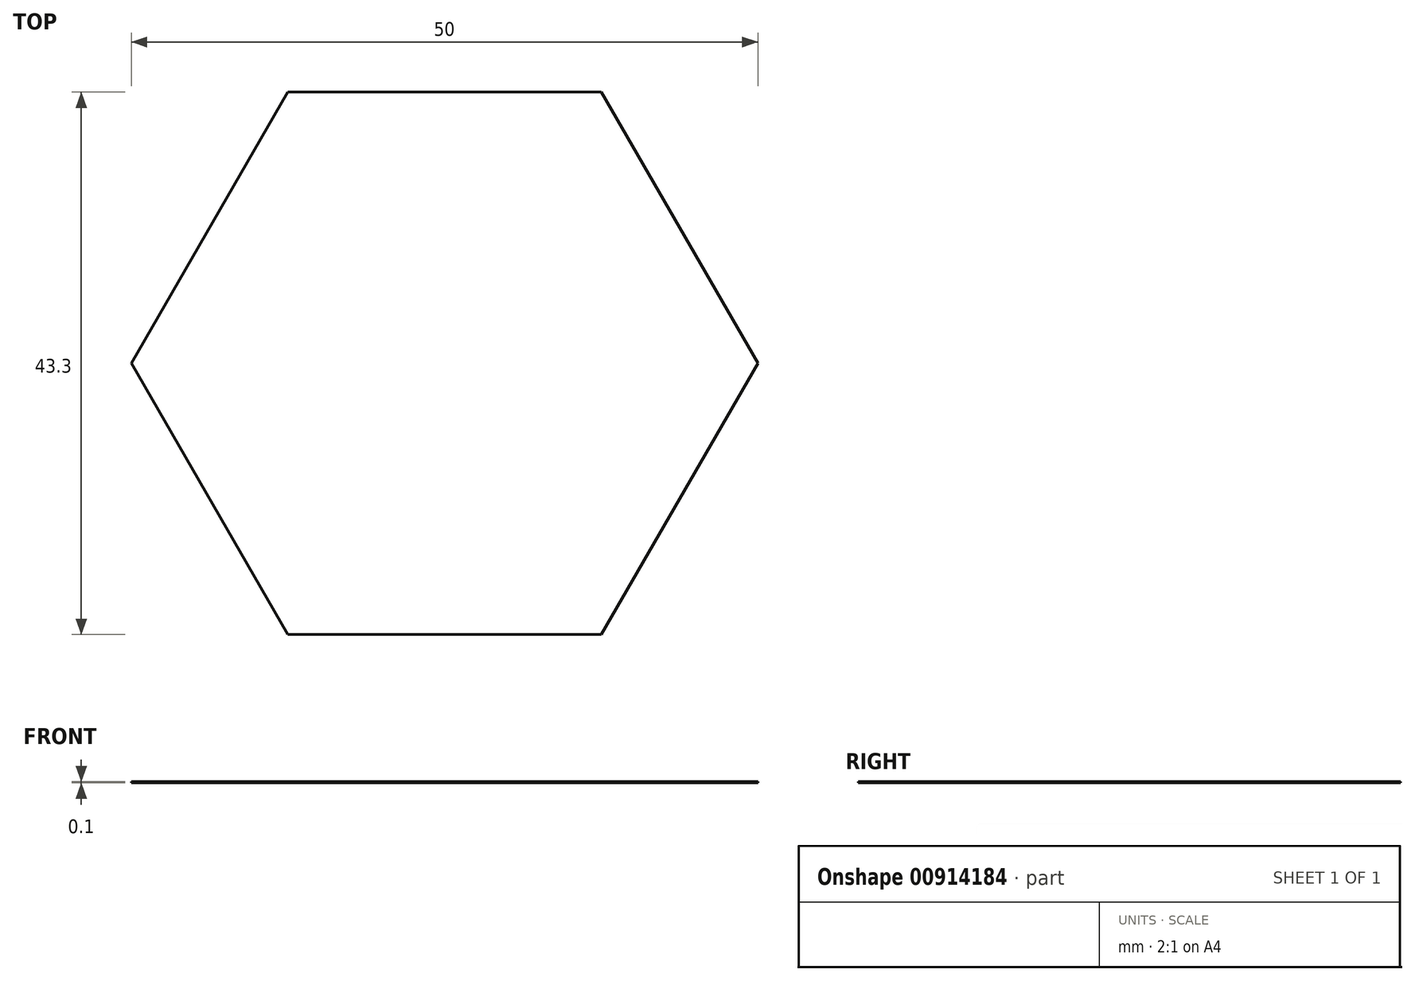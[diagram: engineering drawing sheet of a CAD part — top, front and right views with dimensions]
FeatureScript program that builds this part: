
annotation { "Feature Type Name" : "Feature", "Feature Type Description" : "" }
export const myFeature = defineFeature(function(context is Context, id is Id, definition is map)
    precondition{}
    {
        {
            var Q0;
            Q0=qCreatedBy(makeId("Top.planeOp"),FACE);
            var sketch = newSketch(context, id + "F0", { "sketchPlane" : qUnion([Q0])});
            skCircle(sketch, "E0.cCircle", {"center": v(0, 0) * mm, "radius": 25 * mm, "construction": true});
            skLineSegment(sketch, "E0.0", {"start": v(25, 0) * mm, "end": v(12.5, -21.65) * mm});
            skLineSegment(sketch, "E0.1", {"start": v(12.5, -21.65) * mm, "end": v(-12.5, -21.65) * mm});
            skLineSegment(sketch, "E0.2", {"start": v(-12.5, -21.65) * mm, "end": v(-25, 0) * mm});
            skLineSegment(sketch, "E0.3", {"start": v(-25, 0) * mm, "end": v(-12.5, 21.65) * mm});
            skLineSegment(sketch, "E0.4", {"start": v(-12.5, 21.65) * mm, "end": v(12.5, 21.65) * mm});
            skLineSegment(sketch, "E0.5", {"start": v(12.5, 21.65) * mm, "end": v(25, 0) * mm});
            skSolve(sketch);
        }
        {
            var Q0;
            Q0=makeQuery(id+"F0.imprint","IMPRINT",FACE,{"disambiguationData":[TD([[makeQuery(id+"F0.imprint","IMPRINT",EDGE,{"derivedFrom":sQuery(id+"F0.wireOp",EDGE,"E0.0")}),-1.0]])]});
            extrude(context, id + "F1", {"entities" : qUnion([Q0]), "depth" : 0.1 * mm, "offsetDistance" : 25 * mm});
        }
    });
